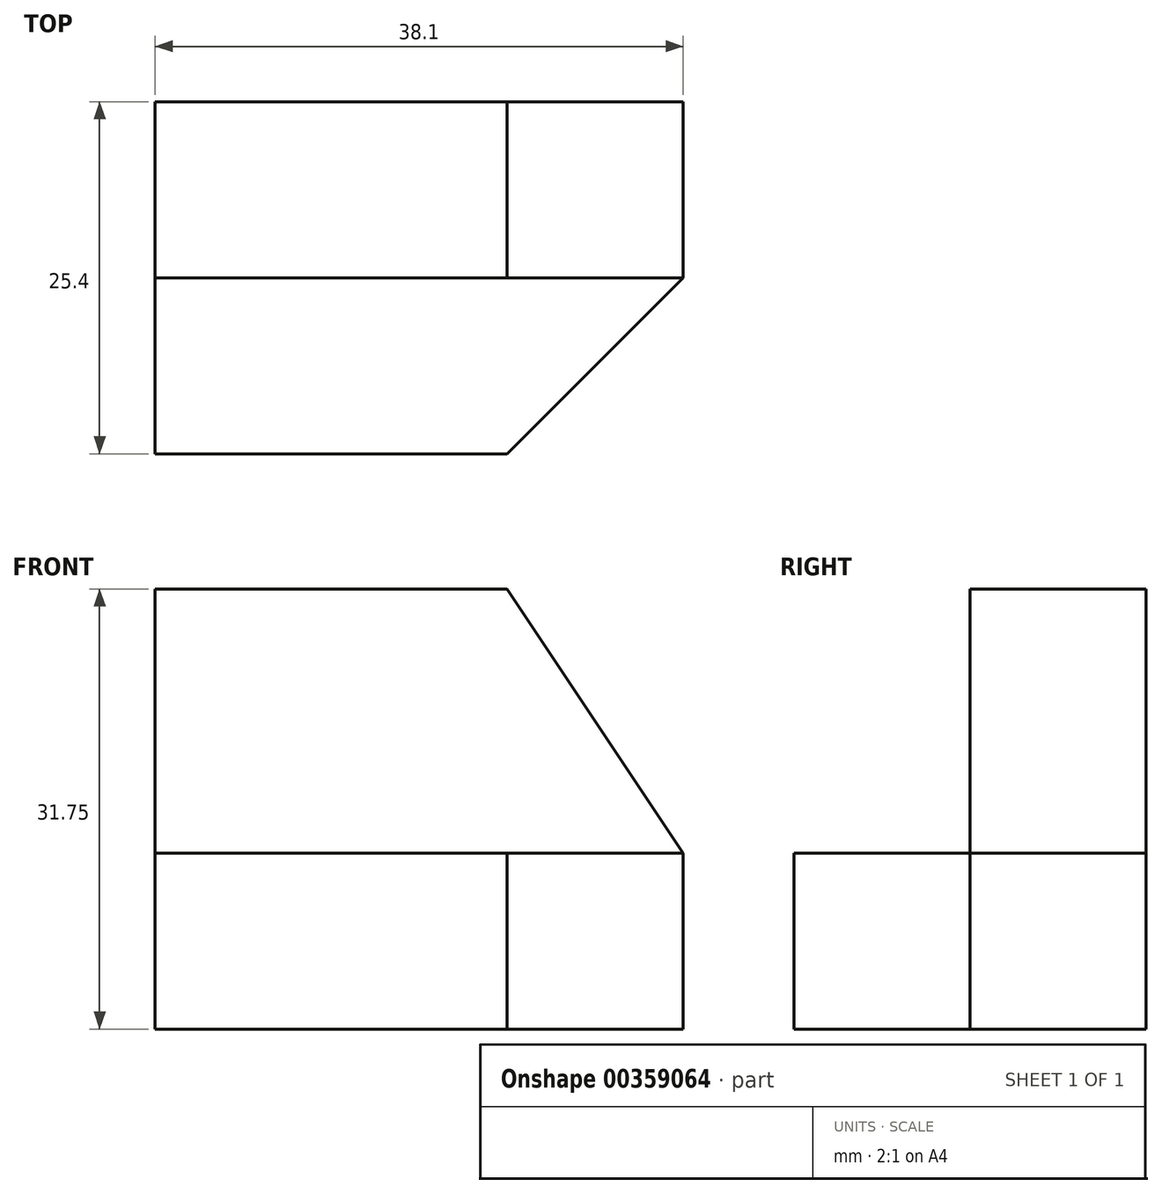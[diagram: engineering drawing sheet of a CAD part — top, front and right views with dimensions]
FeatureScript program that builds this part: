
annotation { "Feature Type Name" : "Feature", "Feature Type Description" : "" }
export const myFeature = defineFeature(function(context is Context, id is Id, definition is map)
    precondition{}
    {
        {
            var Q0;
            Q0=qCreatedBy(makeId("Right.planeOp"),FACE);
            var sketch = newSketch(context, id + "F0", { "sketchPlane" : qUnion([Q0])});
            skLineSegment(sketch, "E0", {"start": v(0, 0) * mm, "end": v(-25.4, 0) * mm});
            skLineSegment(sketch, "E1", {"start": v(-25.4, 0) * mm, "end": v(-25.4, 12.7) * mm});
            skLineSegment(sketch, "E2", {"start": v(-25.4, 12.7) * mm, "end": v(-12.7, 12.7) * mm});
            skLineSegment(sketch, "E3", {"start": v(-12.7, 12.7) * mm, "end": v(-12.7, 31.75) * mm});
            skLineSegment(sketch, "E4", {"start": v(-12.7, 31.75) * mm, "end": v(0, 31.75) * mm});
            skLineSegment(sketch, "E5", {"start": v(0, 31.75) * mm, "end": v(0, 0) * mm});
            skSolve(sketch);
        }
        {
            var Q0;
            Q0 = qSketchRegion(id + "F0", true);
            extrude(context, id + "F1", {"entities" : qUnion([Q0]), "depth" : 38.1 * mm});
        }
        {
            var Q0;
            Q0=makeQuery(id+"F1.opExtrude","SWEPT_FACE",FACE,{"disambiguationData":[OSD([sQuery(id+"F0.wireOp",EDGE,"E3")])]});
            var sketch = newSketch(context, id + "F2", { "sketchPlane" : qUnion([Q0])});
            skLineSegment(sketch, "E6", {"start": v(25.4, 31.75) * mm, "end": v(38.1, 12.7) * mm});
            skLineSegment(sketch, "E7", {"start": v(38.1, 12.7) * mm, "end": v(23.56, 0) * mm});
            skLineSegment(sketch, "E8", {"start": v(25.4, 31.75) * mm, "end": v(38.1, 31.75) * mm});
            skLineSegment(sketch, "E9", {"start": v(38.1, 31.75) * mm, "end": v(38.1, 12.7) * mm});
            skLineSegment(sketch, "E10", {"start": v(38.1, 12.7) * mm, "end": v(38.1, 0) * mm});
            skLineSegment(sketch, "E11", {"start": v(38.1, 0) * mm, "end": v(23.56, 0) * mm});
            skSolve(sketch);
        }
        {
            var Q0;
            Q0=makeQuery(id+"F2.imprint","IMPRINT",FACE,{"disambiguationData":[TD([[makeQuery(id+"F2.imprint","IMPRINT",EDGE,{"derivedFrom":sQuery(id+"F2.wireOp",EDGE,"E6")}),1.0]])]});
            extrude(context, id + "F3", {"entities" : qUnion([Q0]), "operationType" : NewBodyOperationType.REMOVE, "oppositeDirection" : true, "depth" : 25.4 * mm});
        }
        {
            var Q0;
            Q0=makeQuery(id+"F1.opExtrude","SWEPT_FACE",FACE,{"disambiguationData":[OSD([sQuery(id+"F0.wireOp",EDGE,"E2")])]});
            var sketch = newSketch(context, id + "F4", { "sketchPlane" : qUnion([Q0])});
            skLineSegment(sketch, "E12", {"start": v(38.1, -12.7) * mm, "end": v(25.4, -25.4) * mm});
            skLineSegment(sketch, "E13", {"start": v(25.4, -25.4) * mm, "end": v(38.1, -25.4) * mm});
            skLineSegment(sketch, "E14", {"start": v(38.1, -25.4) * mm, "end": v(38.1, -12.7) * mm});
            skSolve(sketch);
        }
        {
            var Q0;
            Q0 = qSketchRegion(id + "F4", true);
            extrude(context, id + "F5", {"entities" : qUnion([Q0]), "operationType" : NewBodyOperationType.REMOVE, "oppositeDirection" : true, "depth" : 25.4 * mm});
        }
    });
